# Revit family: Reggiani Adjustable round flush, M Trim - GG12 8,5W
name_source: partatom
category: Lighting Fixtures
revit_build: Autodesk Revit 2015 (Build: 20140606_1530(x64)
units: mm (PartAtom-declared; Revit-internal decimal feet)

## types (2) — shared parameters
Color Filter = 16777215
Control = Ø. = ON/OFF, D. = DALI, V. = DIMM 1-10V, T
Date of publishing = 2016-09-02
Description = Our adjustable product creates brilliant accent lighting for different environments. The lighting output and aesthetics are of a high standard, featuring multiple optics and a full range of accessories. They are available in various sizes: S, M, L, XL.
Design country = Italy
Dimming Lamp Color Temperature Shift = <None>
Edition number = 1
Lamp = Led
Lens = Policarbonato, Trasparente
Manufacturer = Reggiani Spa Illuminazione
Manufacturer country = Italy
Manufacturer name = Reggiani
Material main = Aluminium
Material secondary = Glass
Model = Reggiani Mood adjustable round flush, GG12B 8,5 W
Nominal height = 120
Nominal width = 80
Photometric Web File = GG12B_HQ_8,5W_11D_ADJ.ies
Product Guid = 3dc5a0f5-5e22-4079-ba44-7a2060405c38
Product SKU = mood_adjustable_round_flush_trim
Product data url = https://bimobject.com
Product family = Recessed fixture
Product group = Mood
QR code = http://bimobject.com
Technical data sheet = http://www.reggiani.net
Technical description = http://www.reggiani.net
Tilt Angle = 90.00°
URL = http://www.reggiani.net
Weight Net (Kg) = 0.26

## per-type parameters (varying)
| type | Frame | Ring Black |
| Reggiani Mood adjustable round flush, M Trim - GG12B 8.5 w White | Reggiani bianco | Reggiani bianco |
| Reggiani Mood adjustable round flush, M Trim - GG12B 8.5 w Black | Reggiani Nero | Reggiani Nero |
